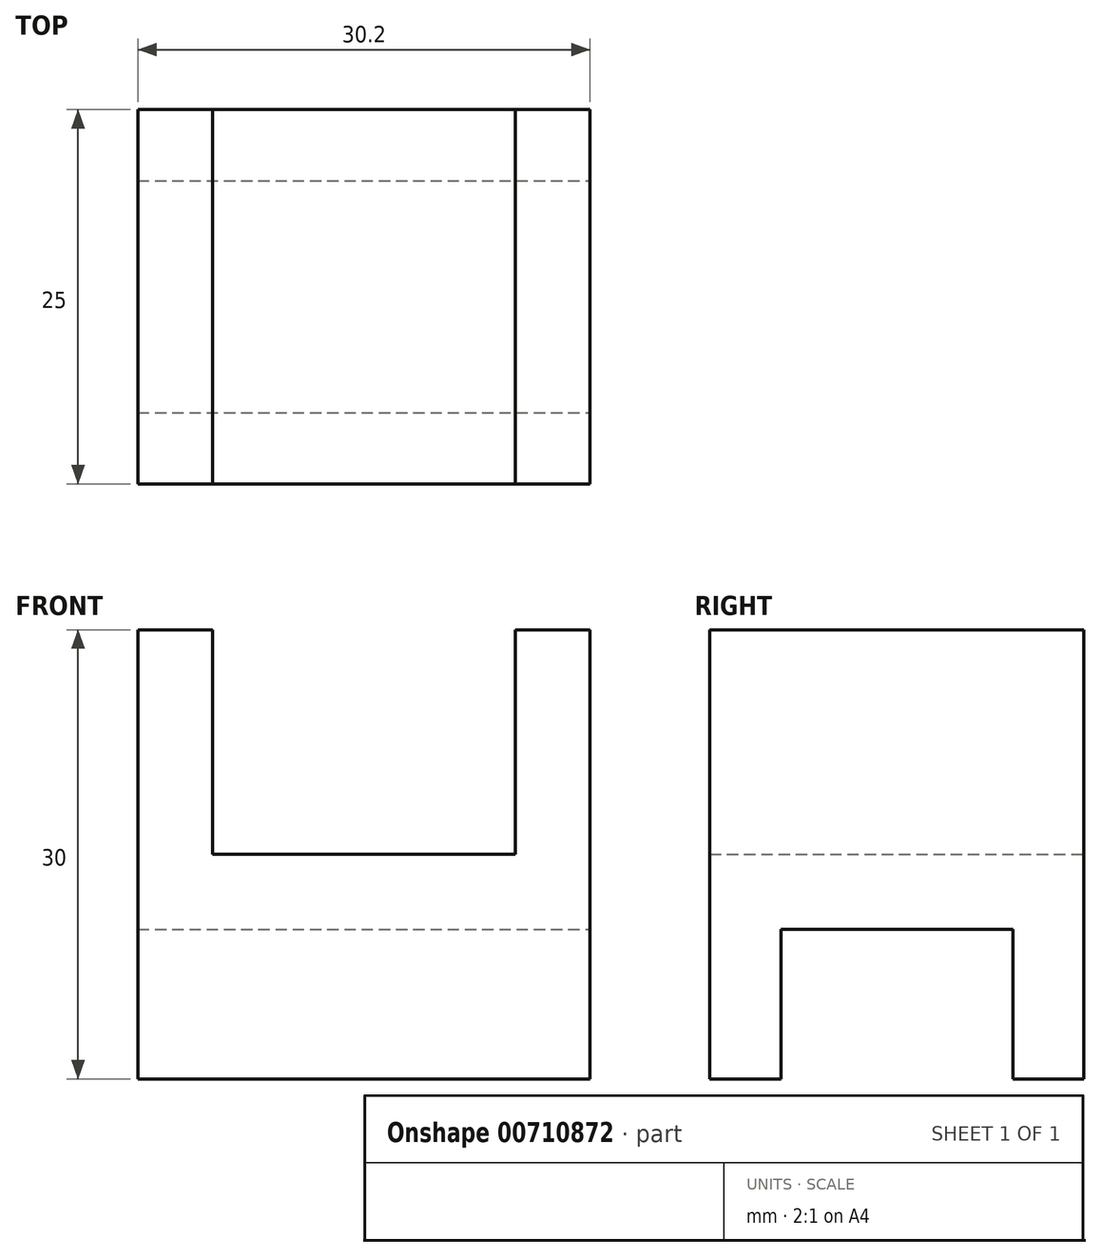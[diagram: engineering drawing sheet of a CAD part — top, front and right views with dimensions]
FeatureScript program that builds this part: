
annotation { "Feature Type Name" : "Feature", "Feature Type Description" : "" }
export const myFeature = defineFeature(function(context is Context, id is Id, definition is map)
    precondition{}
    {
        {
            var Q0;
            Q0=qCreatedBy(makeId("Front.planeOp"),FACE);
            var sketch = newSketch(context, id + "F0", { "sketchPlane" : qUnion([Q0])});
            skLineSegment(sketch, "E0", {"start": v(0, 0) * mm, "end": v(20.2, 0) * mm});
            skLineSegment(sketch, "E1", {"start": v(20.2, 0) * mm, "end": v(20.2, 15) * mm});
            skLineSegment(sketch, "E2", {"start": v(20.2, 15) * mm, "end": v(25.2, 15) * mm});
            skLineSegment(sketch, "E3", {"start": v(25.2, 15) * mm, "end": v(25.2, -15) * mm});
            skLineSegment(sketch, "E4", {"start": v(25.2, -15) * mm, "end": v(-5, -15) * mm});
            skLineSegment(sketch, "E5", {"start": v(-5, -15) * mm, "end": v(-5, 15) * mm});
            skLineSegment(sketch, "E6", {"start": v(-5, 15) * mm, "end": v(0, 15) * mm});
            skLineSegment(sketch, "E7", {"start": v(0, 15) * mm, "end": v(0, 0) * mm});
            skSolve(sketch);
        }
        {
            var Q0;
            Q0 = qSketchRegion(id + "F0", true);
            extrude(context, id + "F1", {"entities" : qUnion([Q0]), "depth" : 25 * mm, "offsetDistance" : 25 * mm});
        }
        {
            var Q0;
            Q0=makeQuery(id+"F1.opExtrude","SWEPT_FACE",FACE,{"disambiguationData":[OSD([sQuery(id+"F0.wireOp",EDGE,"E3")])]});
            var sketch = newSketch(context, id + "F2", { "sketchPlane" : qUnion([Q0])});
            skLineSegment(sketch, "E8", {"start": v(0, -15) * mm, "end": v(-4.75, -15) * mm});
            skLineSegment(sketch, "E9", {"start": v(-4.75, -15) * mm, "end": v(-4.75, -5) * mm});
            skLineSegment(sketch, "E10", {"start": v(-4.75, -5) * mm, "end": v(-20.25, -5) * mm});
            skLineSegment(sketch, "E11", {"start": v(-20.25, -5) * mm, "end": v(-20.25, -15) * mm});
            skLineSegment(sketch, "E12", {"start": v(-20.25, -15) * mm, "end": v(-4.75, -15) * mm});
            skLineSegment(sketch, "E13", {"start": v(-20.25, -15) * mm, "end": v(-25, -15) * mm});
            skSolve(sketch);
        }
        {
            var Q0;
            Q0 = qSketchRegion(id + "F2", true);
            extrude(context, id + "F3", {"entities" : qUnion([Q0]), "operationType" : NewBodyOperationType.REMOVE, "endBound" : BoundingType.UP_TO_NEXT, "oppositeDirection" : true, "depth" : 25 * mm, "offsetDistance" : 25 * mm});
        }
    });
